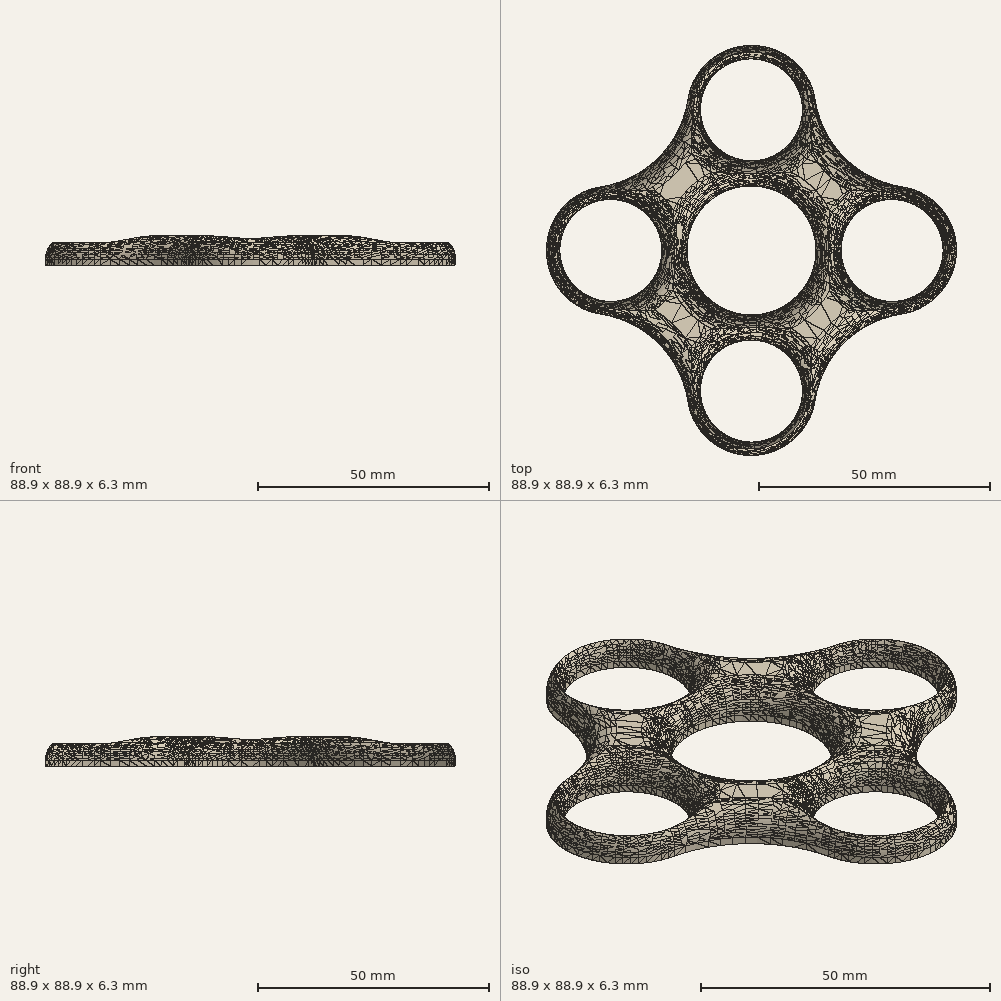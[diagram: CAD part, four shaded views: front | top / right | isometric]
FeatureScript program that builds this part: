
annotation { "Feature Type Name" : "Feature", "Feature Type Description" : "" }
export const myFeature = defineFeature(function(context is Context, id is Id, definition is map)
    precondition{}
    {
        {
            var Q0;
            Q0=qCreatedBy(makeId("Top.planeOp"),FACE);
            var sketch = newSketch(context, id + "F0", { "sketchPlane" : qUnion([Q0])});
            skCircle(sketch, "E0", {"center": v(0, 0) * mm, "radius": 11.05 * mm});
            skCircle(sketch, "E1", {"center": v(0, 0) * mm, "radius": 13.97 * mm});
            skLineSegment(sketch, "E2", {"start": v(0, 0) * mm, "end": v(0, 30.48) * mm});
            skLineSegment(sketch, "E3", {"start": v(0, 0) * mm, "end": v(0, -30.48) * mm});
            skLineSegment(sketch, "E4", {"start": v(0, 0) * mm, "end": v(-30.48, 0) * mm});
            skLineSegment(sketch, "E5", {"start": v(0, 0) * mm, "end": v(30.48, 0) * mm});
            skCircle(sketch, "E6", {"center": v(0, 30.48) * mm, "radius": 11.05 * mm});
            skCircle(sketch, "E7", {"center": v(0, 30.48) * mm, "radius": 13.97 * mm});
            skCircle(sketch, "E8", {"center": v(-30.48, 0) * mm, "radius": 11.05 * mm});
            skCircle(sketch, "E9", {"center": v(30.48, 0) * mm, "radius": 11.05 * mm});
            skCircle(sketch, "E10", {"center": v(0, -30.48) * mm, "radius": 11.05 * mm});
            skCircle(sketch, "E11", {"center": v(-30.48, 0) * mm, "radius": 13.97 * mm});
            skCircle(sketch, "E12", {"center": v(30.48, 0) * mm, "radius": 13.97 * mm});
            skCircle(sketch, "E13", {"center": v(0, -30.48) * mm, "radius": 13.97 * mm});
            skLineSegment(sketch, "E14", {"start": v(0, 0) * mm, "end": v(-35.92, 35.92) * mm});
            skLineSegment(sketch, "E15", {"start": v(0, 0) * mm, "end": v(35.92, 35.92) * mm});
            skLineSegment(sketch, "E16", {"start": v(0, 0) * mm, "end": v(-35.92, -35.92) * mm});
            skLineSegment(sketch, "E17", {"start": v(0, 0) * mm, "end": v(35.92, -35.92) * mm});
            skArc(sketch, "E18", {"start": v(-32.57, 13.81) * mm, "mid": v(-20.1, 20.1) * mm, "end": v(-13.81, 32.57) * mm});
            skArc(sketch, "E19", {"start": v(13.81, 32.57) * mm, "mid": v(20.1, 20.1) * mm, "end": v(32.57, 13.81) * mm});
            skArc(sketch, "E20", {"start": v(32.57, -13.81) * mm, "mid": v(20.1, -20.1) * mm, "end": v(13.81, -32.57) * mm});
            skArc(sketch, "E21", {"start": v(-13.81, -32.57) * mm, "mid": v(-20.1, -20.1) * mm, "end": v(-32.57, -13.81) * mm});
            skSolve(sketch);
        }
        {
            var Q0;
            Q0 = qSketchRegion(id + "F0", true);
            extrude(context, id + "F1", {"entities" : qUnion([Q0]), "depth" : 6.35 * mm, "offsetDistance" : 25.4 * mm});
        }
        {
            var Q0;
            Q0=makeQuery(id+"F1.opExtrude","CAP_FACE",FACE,{"disambiguationData":[OSD([sQuery(id+"F0.wireOp",EDGE,"E1"),sQuery(id+"F0.wireOp",EDGE,"E6"),sQuery(id+"F0.wireOp",EDGE,"E7"),sQuery(id+"F0.wireOp",EDGE,"E8"),sQuery(id+"F0.wireOp",EDGE,"E9"),sQuery(id+"F0.wireOp",EDGE,"E10"),sQuery(id+"F0.wireOp",EDGE,"E11"),sQuery(id+"F0.wireOp",EDGE,"E12"),sQuery(id+"F0.wireOp",EDGE,"E13"),sQuery(id+"F0.wireOp",EDGE,"E18"),sQuery(id+"F0.wireOp",EDGE,"E19"),sQuery(id+"F0.wireOp",EDGE,"E20"),sQuery(id+"F0.wireOp",EDGE,"E21")])],"isStart":false});
            fillet(context, id + "F2", {"entities" : qUnion([Q0]), "radius" : 5.08 * mm, "tangentPropagation" : true, "allowEdgeOverflow" : false});
        }
    });
